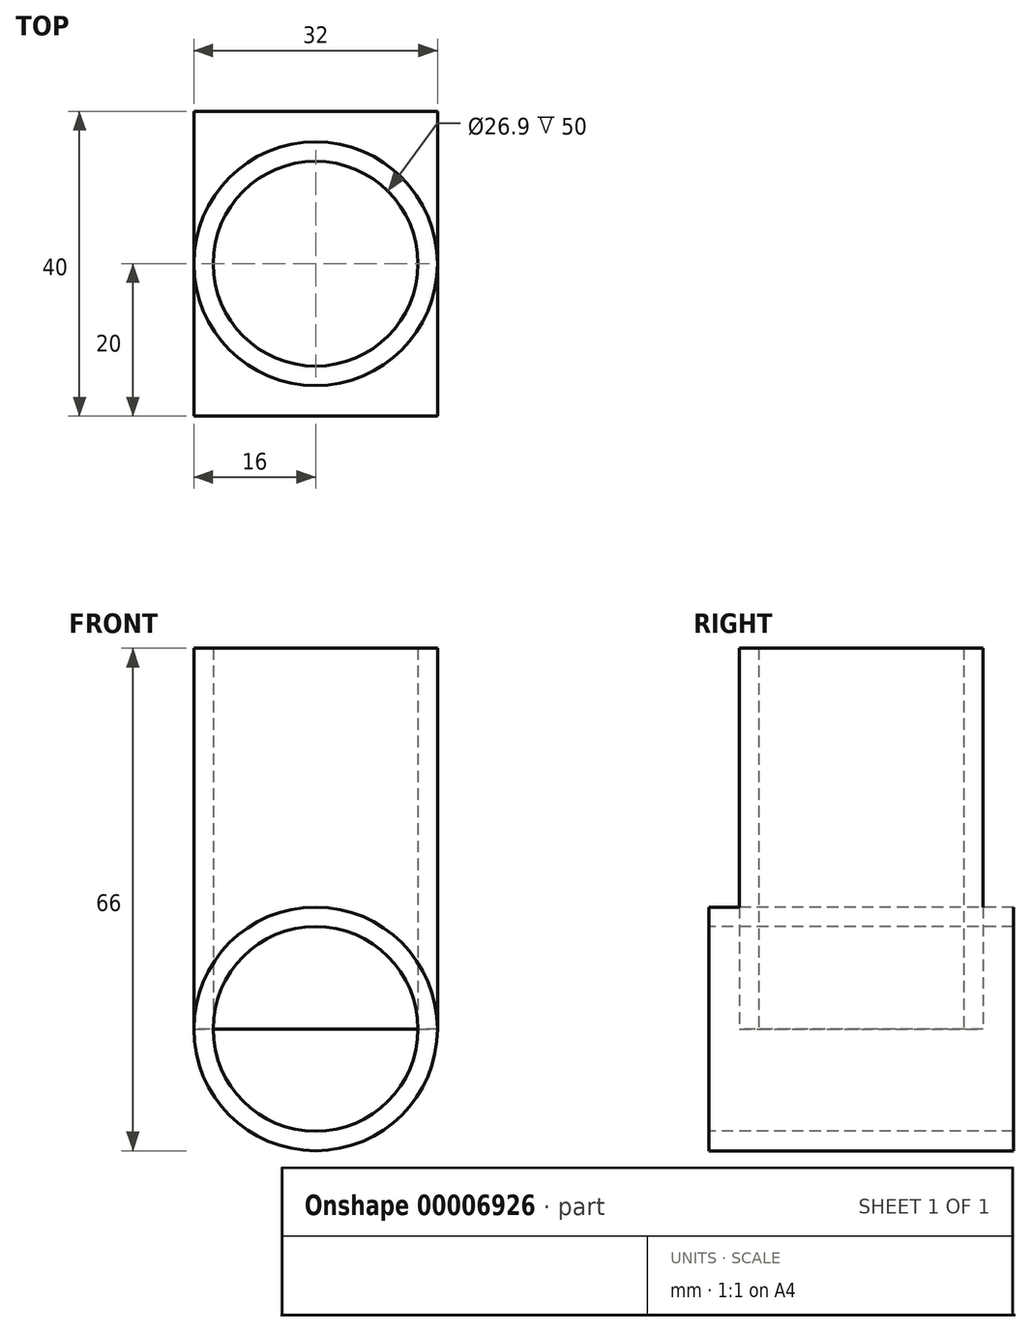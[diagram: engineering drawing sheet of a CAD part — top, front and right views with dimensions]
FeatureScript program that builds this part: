
annotation { "Feature Type Name" : "Feature", "Feature Type Description" : "" }
export const myFeature = defineFeature(function(context is Context, id is Id, definition is map)
    precondition{}
    {
        {
            var Q0;
            Q0=qCreatedBy(makeId("Top.planeOp"),FACE);
            var sketch = newSketch(context, id + "F0", { "sketchPlane" : qUnion([Q0])});
            skCircle(sketch, "E0", {"center": v(0, 0) * mm, "radius": 13.45 * mm});
            skCircle(sketch, "E1", {"center": v(0, 0) * mm, "radius": 16 * mm});
            skSolve(sketch);
        }
        {
            var Q0;
            Q0=makeQuery(id+"F0.imprint","IMPRINT",FACE,{"disambiguationData":[TD([[makeQuery(id+"F0.imprint","IMPRINT",EDGE,{"derivedFrom":sQuery(id+"F0.wireOp",EDGE,"E0")}),-1.0]])]});
            extrude(context, id + "F1", {"entities" : qUnion([Q0]), "depth" : 50 * mm});
        }
        {
            var Q0;
            Q0=qCreatedBy(makeId("Front.planeOp"),FACE);
            cPlane(context, id + "F2", {"entities" : qUnion([Q0]), "cplaneType" : CPlaneType.OFFSET, "offset" : 20 * mm, "width" : 150 * mm, "height" : 150 * mm});
        }
        {
            var Q0;
            Q0=qCreatedBy(id+"F2.planeOp",FACE);
            var sketch = newSketch(context, id + "F3", { "sketchPlane" : qUnion([Q0])});
            skCircle(sketch, "E2", {"center": v(0, 0) * mm, "radius": 16 * mm});
            skCircle(sketch, "E3", {"center": v(0, 0) * mm, "radius": 13.45 * mm});
            skSolve(sketch);
        }
        {
            var Q0;
            Q0 = qSketchRegion(id + "F3", true);
            extrude(context, id + "F4", {"entities" : qUnion([Q0]), "oppositeDirection" : true, "depth" : 40 * mm});
        }
    });
